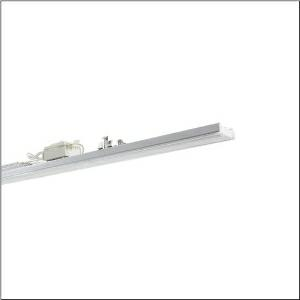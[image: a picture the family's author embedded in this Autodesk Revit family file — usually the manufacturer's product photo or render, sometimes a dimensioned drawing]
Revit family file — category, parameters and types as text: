
# Revit family: licross_21_recessed_mo_51te18vn465g
name_source: partatom
category: Lighting Fixtures
units: mm (PartAtom-declared; Revit-internal decimal feet)

## family parameters
Cut with Voids When Loaded = No
Host = Face
Light Source = No
Part Type = Normal
Room Calculation Point = No
Round Connector Dimension = Use Diameter
Shared = No

## types (1)
- --- (1 x LED, 6500 lm, 35.3 W, 4000K)
    Apparent Load = 35 VA
    CIE Flux Codes = 83 96 99 100 100
    Color Rendering = 80
    Color Temperature = 4000K
    Default Elevation = 1800 mm
    Description = Licross 21 Recessed MO, luminaire insert, of sheet steel, galvanised, coil coated, white, length: 1.500mm, width: 66mm, height: 67mm, LED rated luminous flux: 6.500lm, light colour: 840, SDCM (Standard Deviation of Colour Matching)MacAdam ≤ 2 SDCM (initial), control gear: DALI 2, CLO, with plug, 5-pole, with phase selection, mains connection: 220..240V, AC, 50/60Hz, start of lifetime: 35W, end of service life: 39W, internal wiring halogen-free, primary light control with lens, of plastic, primary optical cover: cover, of PMMA, light emission: direct distribution, primary light characteristic: symmetric, protection rating (complete): IP54, insulation class (complete): insulation class I (protective earthing), certification: CE, ENEC, VDE, UKCA, protection symbol: D if used in an environment with non-conductive dust loads with corresponding accessories, impact resistance: IK06, permissible ambient temperature for indoor applications: -25..+40°C, corresponds to IFS (International Featured Standards) requirements for safety and quality in the food industry, reducing of maximum allowable ambient temperature of 5°C with ceiling mounting, LABS conformity tested according to VDMA 24364:2018-05, The light source and the operating device comply with the requirements of the Ecodesign Regulation (EU) 2019/2020 and are replaceable in accordance with this regulation, packaging unit: 1 piece
    Height = 58 mm
    Lamp = 1 x LED
    Lamp Light Flux = 6500 lm
    Lamp Power = 35.3 W
    Lamp count = 1
    Length = 1500 mm
    Luminous efficacy = 184 lm/W
    Manufacturer = Siteco
    ModVariant = No
    Model = 51TE18VN465G
    Mounting Place = Ceiling
    Mounting Type = Pendant
    Number of Poles = 1
    OnlyDefault = Yes
    Power Factor = 1
    Product Name = Licross 21 Recessed MO
    Product group = luminaire insert | ceiling pendant
    ProductGroupID = 901
    Protection Class = Protection class I
    Protection Degree = IP 54
    RLX_Detail_Level = 1
    RLX_Emergency_Light_Flux = 0 lm
    RLX_Emergency_Type = 0
    RLX_Emergency_Type_DB = No
    RlxData = <blob elided: 24633 chars, md5=762144e8>
    Socket = socket
    Standby Power = 0 W
    System Light Flux = 6500 lm
    System Power = 35 W
    Type Comments = factory setting: luminous flux: 100 % | dim-lin: 254 | 239 mA
    Type Image = l_1296930.jpg
    URL = http://relux.com
    VarID = @adj_092399
    Voltage = 0 V
    Weight = 0.00 kg
    Width = 66 mm

## geometry (parser evidence)
native form markers: Blend x4, Sweep x9
no freeform markers — native parametric forms only
